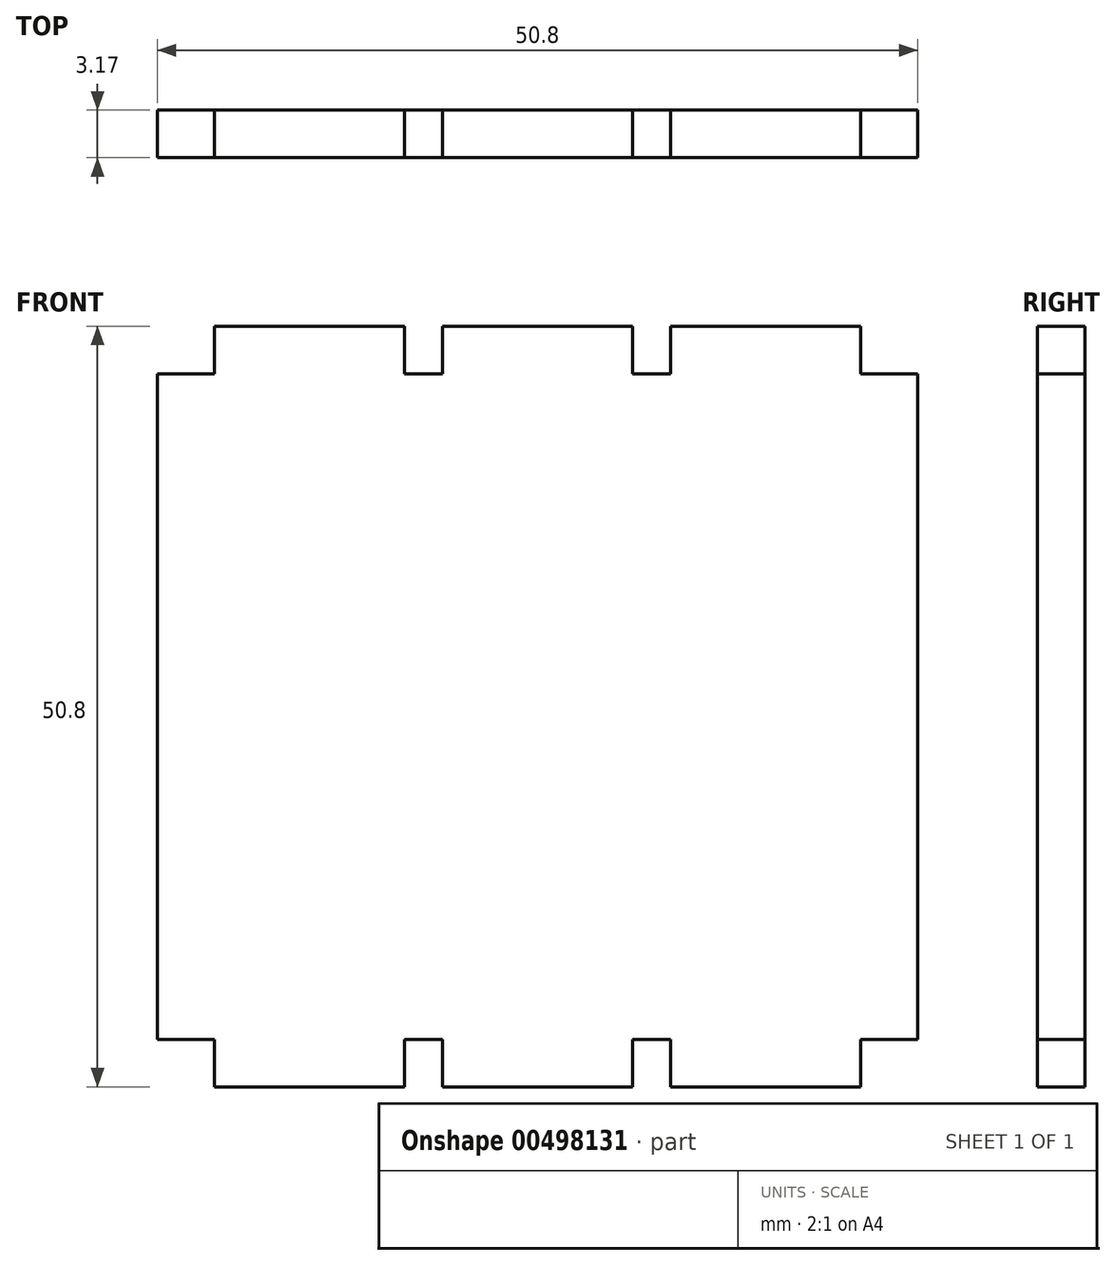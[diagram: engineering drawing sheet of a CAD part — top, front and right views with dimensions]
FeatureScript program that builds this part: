
annotation { "Feature Type Name" : "Feature", "Feature Type Description" : "" }
export const myFeature = defineFeature(function(context is Context, id is Id, definition is map)
    precondition{}
    {
        {
            var Q0;
            Q0=qCreatedBy(makeId("Front.planeOp"),FACE);
            var sketch = newSketch(context, id + "F0", { "sketchPlane" : qUnion([Q0])});
            skPoint(sketch, "E0.middle", {"position": v(0, 0) * mm});
            skLineSegment(sketch, "E1", {"start": v(25.4, -22.22) * mm, "end": v(21.6, -22.22) * mm});
            skLineSegment(sketch, "E2", {"start": v(21.6, -22.22) * mm, "end": v(21.6, -25.4) * mm});
            skLineSegment(sketch, "E3", {"start": v(8.9, -25.4) * mm, "end": v(8.9, -22.23) * mm});
            skLineSegment(sketch, "E4.MirrorCS", {"start": v(-8.9, -25.4) * mm, "end": v(-8.9, -22.23) * mm});
            skLineSegment(sketch, "E5.MirrorCS", {"start": v(-21.6, -22.22) * mm, "end": v(-21.6, -25.4) * mm});
            skLineSegment(sketch, "E6.MirrorCS", {"start": v(-25.4, -22.22) * mm, "end": v(-21.6, -22.22) * mm});
            skLineSegment(sketch, "E7.MirrorCS", {"start": v(6.35, -25.4) * mm, "end": v(6.35, -22.23) * mm});
            skLineSegment(sketch, "E8.MirrorCS", {"start": v(-6.35, -22.23) * mm, "end": v(-6.35, -25.4) * mm});
            skLineSegment(sketch, "E9", {"start": v(-8.9, -22.23) * mm, "end": v(-6.35, -22.23) * mm});
            skLineSegment(sketch, "E10", {"start": v(6.35, -22.23) * mm, "end": v(8.9, -22.23) * mm});
            skLineSegment(sketch, "E11.MirrorCS", {"start": v(6.35, 22.23) * mm, "end": v(8.9, 22.23) * mm});
            skLineSegment(sketch, "E12.MirrorCS", {"start": v(-8.9, 22.23) * mm, "end": v(-6.35, 22.23) * mm});
            skLineSegment(sketch, "E13.MirrorCS", {"start": v(-8.9, 25.4) * mm, "end": v(-8.9, 22.23) * mm});
            skLineSegment(sketch, "E14.MirrorCS", {"start": v(6.35, 25.4) * mm, "end": v(6.35, 22.23) * mm});
            skLineSegment(sketch, "E15.MirrorCS", {"start": v(8.9, 25.4) * mm, "end": v(8.9, 22.23) * mm});
            skLineSegment(sketch, "E16.MirrorCS", {"start": v(-6.35, 22.23) * mm, "end": v(-6.35, 25.4) * mm});
            skLineSegment(sketch, "E17.MirrorCS", {"start": v(-25.4, 22.22) * mm, "end": v(-21.6, 22.22) * mm});
            skLineSegment(sketch, "E18.MirrorCS", {"start": v(25.4, 22.22) * mm, "end": v(21.6, 22.22) * mm});
            skLineSegment(sketch, "E19.MirrorCS", {"start": v(21.6, 22.22) * mm, "end": v(21.6, 25.4) * mm});
            skLineSegment(sketch, "E20.MirrorCS", {"start": v(-21.6, 22.22) * mm, "end": v(-21.6, 25.4) * mm});
            skLineSegment(sketch, "E21", {"start": v(-25.4, 22.22) * mm, "end": v(-25.4, -22.22) * mm});
            skLineSegment(sketch, "E22", {"start": v(25.4, 22.22) * mm, "end": v(25.4, -22.22) * mm});
            skLineSegment(sketch, "E23", {"start": v(-21.6, -25.4) * mm, "end": v(-8.9, -25.4) * mm});
            skLineSegment(sketch, "E24", {"start": v(-6.35, -25.4) * mm, "end": v(6.35, -25.4) * mm});
            skLineSegment(sketch, "E25", {"start": v(8.9, -25.4) * mm, "end": v(21.6, -25.4) * mm});
            skLineSegment(sketch, "E26", {"start": v(21.6, 25.4) * mm, "end": v(8.9, 25.4) * mm});
            skLineSegment(sketch, "E27", {"start": v(6.35, 25.4) * mm, "end": v(-6.35, 25.4) * mm});
            skLineSegment(sketch, "E28", {"start": v(-8.9, 25.4) * mm, "end": v(-21.6, 25.4) * mm});
            skSolve(sketch);
        }
        {
            var Q0;
            Q0=makeQuery(id+"F0.imprint","IMPRINT",FACE,{"disambiguationData":[TD([[makeQuery(id+"F0.imprint","IMPRINT",EDGE,{"derivedFrom":sQuery(id+"F0.wireOp",EDGE,"E1")}),-1.0]])]});
            extrude(context, id + "F1", {"entities" : qUnion([Q0]), "depth" : 3.17 * mm, "offsetDistance" : 25.4 * mm});
        }
    });
